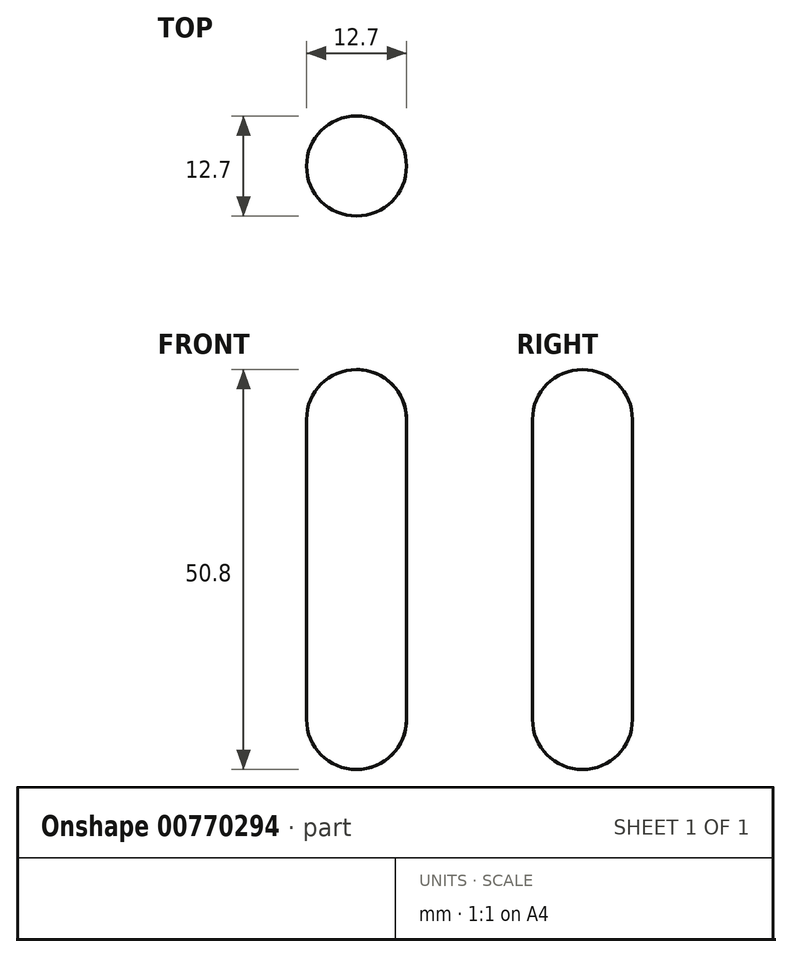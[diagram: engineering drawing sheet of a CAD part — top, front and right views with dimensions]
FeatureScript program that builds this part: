
annotation { "Feature Type Name" : "Feature", "Feature Type Description" : "" }
export const myFeature = defineFeature(function(context is Context, id is Id, definition is map)
    precondition{}
    {
        {
            var Q0;
            Q0=qCreatedBy(makeId("Top.planeOp"),FACE);
            var sketch = newSketch(context, id + "F0", { "sketchPlane" : qUnion([Q0])});
            skCircle(sketch, "E0", {"center": v(0, 0) * mm, "radius": 6.35 * mm});
            skSolve(sketch);
        }
        {
            var Q0;
            Q0=makeQuery(id+"F0.imprint","IMPRINT",FACE,{"disambiguationData":[TD([[makeQuery(id+"F0.imprint","IMPRINT",EDGE,{"derivedFrom":sQuery(id+"F0.wireOp",EDGE,"E0")}),1.0]])]});
            var Q1;
            Q1=sQuery(id+"F0.wireOp",EDGE,"E0");
            extrude(context, id + "F1", {"entities" : qUnion([Q0]), "surfaceEntities" : qUnion([Q1]), "depth" : 25.4 * mm, "offsetDistance" : 25.4 * mm});
        }
        {
            var Q0;
            Q0=makeQuery(id+"F1.opExtrude","CAP_EDGE",EDGE,{"disambiguationData":[OSD([sQuery(id+"F0.wireOp",EDGE,"E0")])],"isStart":false});
            fillet(context, id + "F2", {"entities" : qUnion([Q0]), "radius" : 6.35 * mm, "tangentPropagation" : true, "allowEdgeOverflow" : false});
        }
        {
            var Q0;
            Q0=makeQuery(id+"F1.opExtrude","SWEPT_BODY",BODY,{"disambiguationData":[OSD([sQuery(id+"F0.wireOp",EDGE,"E0")])]});
            var Q1;
            Q1=makeQuery(id+"F1.opExtrude","CAP_FACE",FACE,{"disambiguationData":[OSD([sQuery(id+"F0.wireOp",EDGE,"E0")])],"isStart":true});
            mirror(context, id + "F3", {"operationType" : NewBodyOperationType.ADD, "entities" : qUnion([Q0]), "mirrorPlane" : qUnion([Q1])});
        }
    });
